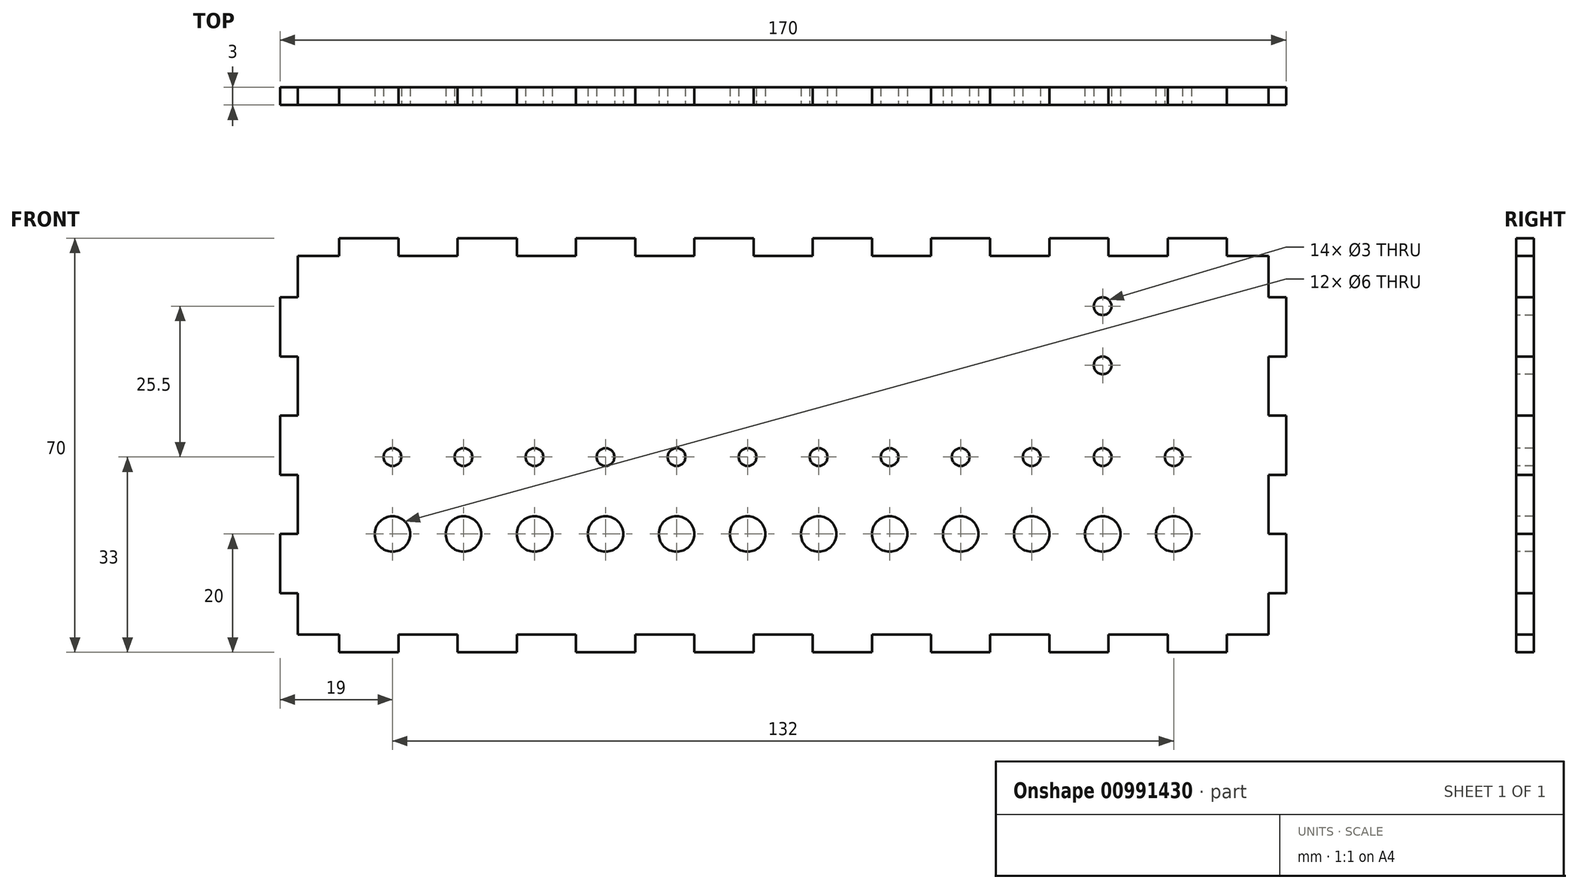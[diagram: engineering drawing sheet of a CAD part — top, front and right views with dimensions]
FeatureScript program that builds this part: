
annotation { "Feature Type Name" : "Feature", "Feature Type Description" : "" }
export const myFeature = defineFeature(function(context is Context, id is Id, definition is map)
    precondition{}
    {
        {
            var Q0;
            Q0=qCreatedBy(makeId("Front.planeOp"),FACE);
            var sketch = newSketch(context, id + "F0", { "sketchPlane" : qUnion([Q0])});
            skLineSegment(sketch, "E0.bottom", {"start": v(85, -35) * mm, "end": v(-85, -35) * mm});
            skLineSegment(sketch, "E0.top", {"start": v(85, 35) * mm, "end": v(-85, 35) * mm});
            skLineSegment(sketch, "E0.left", {"start": v(85, -35) * mm, "end": v(85, 35) * mm});
            skLineSegment(sketch, "E0.right", {"start": v(-85, -35) * mm, "end": v(-85, 35) * mm});
            skPoint(sketch, "E0.middle", {"position": v(0, 0) * mm});
            skSolve(sketch);
        }
        {
            var Q0;
            Q0=makeQuery(id+"F0.imprint","IMPRINT",FACE,{"disambiguationData":[TD([[makeQuery(id+"F0.imprint","IMPRINT",EDGE,{"derivedFrom":sQuery(id+"F0.wireOp",EDGE,"E0.bottom")}),-1.0]])]});
            extrude(context, id + "F1", {"entities" : qUnion([Q0]), "depth" : 3 * mm, "offsetDistance" : 25 * mm});
        }
        {
            var Q0;
            Q0=makeQuery(id+"F1.opExtrude","CAP_FACE",FACE,{"disambiguationData":[OSD([sQuery(id+"F0.wireOp",EDGE,"E0.bottom"),sQuery(id+"F0.wireOp",EDGE,"E0.top"),sQuery(id+"F0.wireOp",EDGE,"E0.left"),sQuery(id+"F0.wireOp",EDGE,"E0.right")])],"isStart":false});
            var sketch = newSketch(context, id + "F2", { "sketchPlane" : qUnion([Q0])});
            skLineSegment(sketch, "E1", {"start": v(-85, -15) * mm, "end": v(85, -15) * mm, "construction": true});
            skCircle(sketch, "E2", {"center": v(66, -15) * mm, "radius": 3 * mm});
            skCircle(sketch, "E3.1.0.0", {"center": v(54, -15) * mm, "radius": 3 * mm});
            skCircle(sketch, "E3.2.0.0", {"center": v(42, -15) * mm, "radius": 3 * mm});
            skCircle(sketch, "E3.3.0.0", {"center": v(30, -15) * mm, "radius": 3 * mm});
            skCircle(sketch, "E3.4.0.0", {"center": v(18, -15) * mm, "radius": 3 * mm});
            skCircle(sketch, "E3.5.0.0", {"center": v(6, -15) * mm, "radius": 3 * mm});
            skCircle(sketch, "E3.6.0.0", {"center": v(-6, -15) * mm, "radius": 3 * mm});
            skCircle(sketch, "E3.7.0.0", {"center": v(-18, -15) * mm, "radius": 3 * mm});
            skCircle(sketch, "E3.8.0.0", {"center": v(-30, -15) * mm, "radius": 3 * mm});
            skCircle(sketch, "E3.9.0.0", {"center": v(-42, -15) * mm, "radius": 3 * mm});
            skCircle(sketch, "E3.10.0.0", {"center": v(-54, -15) * mm, "radius": 3 * mm});
            skCircle(sketch, "E3.11.0.0", {"center": v(-66, -15) * mm, "radius": 3 * mm});
            skLineSegment(sketch, "E3.direction1", {"start": v(66, -15) * mm, "end": v(54, -15) * mm, "construction": true});
            skSolve(sketch);
        }
        {
            var Q0;
            Q0 = qSketchRegion(id + "F2", true);
            extrude(context, id + "F3", {"entities" : qUnion([Q0]), "operationType" : NewBodyOperationType.REMOVE, "endBound" : BoundingType.THROUGH_ALL, "oppositeDirection" : true, "depth" : 25 * mm, "offsetDistance" : 25 * mm});
        }
        {
            var Q0;
            Q0=makeQuery(id+"F1.opExtrude","CAP_FACE",FACE,{"disambiguationData":[OSD([sQuery(id+"F0.wireOp",EDGE,"E0.bottom"),sQuery(id+"F0.wireOp",EDGE,"E0.top"),sQuery(id+"F0.wireOp",EDGE,"E0.left"),sQuery(id+"F0.wireOp",EDGE,"E0.right")])],"isStart":false});
            var sketch = newSketch(context, id + "F4", { "sketchPlane" : qUnion([Q0])});
            skLineSegment(sketch, "E4", {"start": v(-85, -2) * mm, "end": v(85, -2) * mm, "construction": true});
            skLineSegment(sketch, "E5", {"start": v(-66, -15) * mm, "end": v(-66, -2) * mm, "construction": true});
            skCircle(sketch, "E6", {"center": v(-66, -2) * mm, "radius": 1.5 * mm});
            skCircle(sketch, "E7.1.0.0", {"center": v(-54, -2) * mm, "radius": 1.5 * mm});
            skCircle(sketch, "E7.2.0.0", {"center": v(-42, -2) * mm, "radius": 1.5 * mm});
            skCircle(sketch, "E7.3.0.0", {"center": v(-30, -2) * mm, "radius": 1.5 * mm});
            skCircle(sketch, "E7.4.0.0", {"center": v(-18, -2) * mm, "radius": 1.5 * mm});
            skCircle(sketch, "E7.5.0.0", {"center": v(-6, -2) * mm, "radius": 1.5 * mm});
            skCircle(sketch, "E7.6.0.0", {"center": v(6, -2) * mm, "radius": 1.5 * mm});
            skCircle(sketch, "E7.7.0.0", {"center": v(18, -2) * mm, "radius": 1.5 * mm});
            skCircle(sketch, "E7.8.0.0", {"center": v(30, -2) * mm, "radius": 1.5 * mm});
            skCircle(sketch, "E7.9.0.0", {"center": v(42, -2) * mm, "radius": 1.5 * mm});
            skCircle(sketch, "E7.10.0.0", {"center": v(54, -2) * mm, "radius": 1.5 * mm});
            skCircle(sketch, "E7.11.0.0", {"center": v(66, -2) * mm, "radius": 1.5 * mm});
            skLineSegment(sketch, "E7.direction1", {"start": v(-66, -2) * mm, "end": v(-54, -2) * mm, "construction": true});
            skSolve(sketch);
        }
        {
            var Q0;
            Q0 = qSketchRegion(id + "F4", true);
            extrude(context, id + "F5", {"entities" : qUnion([Q0]), "operationType" : NewBodyOperationType.REMOVE, "endBound" : BoundingType.THROUGH_ALL, "oppositeDirection" : true, "depth" : 25 * mm, "offsetDistance" : 25 * mm});
        }
        {
            var Q0;
            Q0=makeQuery(id+"F1.opExtrude","CAP_FACE",FACE,{"disambiguationData":[OSD([sQuery(id+"F0.wireOp",EDGE,"E0.bottom"),sQuery(id+"F0.wireOp",EDGE,"E0.top"),sQuery(id+"F0.wireOp",EDGE,"E0.left"),sQuery(id+"F0.wireOp",EDGE,"E0.right")])],"isStart":false});
            var sketch = newSketch(context, id + "F6", { "sketchPlane" : qUnion([Q0])});
            skLineSegment(sketch, "E8", {"start": v(54, -2) * mm, "end": v(54, 8.14) * mm, "construction": true});
            skCircle(sketch, "E9", {"center": v(54, 13.5) * mm, "radius": 1.5 * mm});
            skCircle(sketch, "E10.0.1.0", {"center": v(54, 23.5) * mm, "radius": 1.5 * mm});
            skLineSegment(sketch, "E10.direction1", {"start": v(54, 13.5) * mm, "end": v(79, 13.5) * mm, "construction": true});
            skLineSegment(sketch, "E10.direction2", {"start": v(54, 13.5) * mm, "end": v(54, 23.5) * mm, "construction": true});
            skSolve(sketch);
        }
        {
            var Q0;
            Q0 = qSketchRegion(id + "F6", true);
            extrude(context, id + "F7", {"entities" : qUnion([Q0]), "operationType" : NewBodyOperationType.REMOVE, "endBound" : BoundingType.THROUGH_ALL, "oppositeDirection" : true, "depth" : 25 * mm, "offsetDistance" : 25 * mm});
        }
        {
            var Q0;
            Q0=makeQuery(id+"F1.opExtrude","CAP_FACE",FACE,{"disambiguationData":[OSD([sQuery(id+"F0.wireOp",EDGE,"E0.bottom"),sQuery(id+"F0.wireOp",EDGE,"E0.top"),sQuery(id+"F0.wireOp",EDGE,"E0.left"),sQuery(id+"F0.wireOp",EDGE,"E0.right")])],"isStart":false});
            var sketch = newSketch(context, id + "F8", { "sketchPlane" : qUnion([Q0])});
            skLineSegment(sketch, "E11.bottom", {"start": v(-85, -35) * mm, "end": v(-75, -35) * mm});
            skLineSegment(sketch, "E11.top", {"start": v(-85, -32) * mm, "end": v(-75, -32) * mm});
            skLineSegment(sketch, "E11.left", {"start": v(-85, -35) * mm, "end": v(-85, -32) * mm});
            skLineSegment(sketch, "E11.right", {"start": v(-75, -35) * mm, "end": v(-75, -32) * mm});
            skLineSegment(sketch, "E12.1.0.0", {"start": v(-55, -35) * mm, "end": v(-55, -32) * mm});
            skLineSegment(sketch, "E12.1.0.1", {"start": v(-65, -35) * mm, "end": v(-65, -32) * mm});
            skLineSegment(sketch, "E12.1.0.2", {"start": v(-65, -35) * mm, "end": v(-55, -35) * mm});
            skLineSegment(sketch, "E12.1.0.3", {"start": v(-65, -32) * mm, "end": v(-55, -32) * mm});
            skLineSegment(sketch, "E12.2.0.0", {"start": v(-35, -35) * mm, "end": v(-35, -32) * mm});
            skLineSegment(sketch, "E12.2.0.1", {"start": v(-45, -35) * mm, "end": v(-45, -32) * mm});
            skLineSegment(sketch, "E12.2.0.2", {"start": v(-45, -35) * mm, "end": v(-35, -35) * mm});
            skLineSegment(sketch, "E12.2.0.3", {"start": v(-45, -32) * mm, "end": v(-35, -32) * mm});
            skLineSegment(sketch, "E12.3.0.0", {"start": v(-15, -35) * mm, "end": v(-15, -32) * mm});
            skLineSegment(sketch, "E12.3.0.1", {"start": v(-25, -35) * mm, "end": v(-25, -32) * mm});
            skLineSegment(sketch, "E12.3.0.2", {"start": v(-25, -35) * mm, "end": v(-15, -35) * mm});
            skLineSegment(sketch, "E12.3.0.3", {"start": v(-25, -32) * mm, "end": v(-15, -32) * mm});
            skLineSegment(sketch, "E12.4.0.0", {"start": v(5, -35) * mm, "end": v(5, -32) * mm});
            skLineSegment(sketch, "E12.4.0.1", {"start": v(-5, -35) * mm, "end": v(-5, -32) * mm});
            skLineSegment(sketch, "E12.4.0.2", {"start": v(-5, -35) * mm, "end": v(5, -35) * mm});
            skLineSegment(sketch, "E12.4.0.3", {"start": v(-5, -32) * mm, "end": v(5, -32) * mm});
            skLineSegment(sketch, "E12.5.0.0", {"start": v(25, -35) * mm, "end": v(25, -32) * mm});
            skLineSegment(sketch, "E12.5.0.1", {"start": v(15, -35) * mm, "end": v(15, -32) * mm});
            skLineSegment(sketch, "E12.5.0.2", {"start": v(15, -35) * mm, "end": v(25, -35) * mm});
            skLineSegment(sketch, "E12.5.0.3", {"start": v(15, -32) * mm, "end": v(25, -32) * mm});
            skLineSegment(sketch, "E12.6.0.0", {"start": v(45, -35) * mm, "end": v(45, -32) * mm});
            skLineSegment(sketch, "E12.6.0.1", {"start": v(35, -35) * mm, "end": v(35, -32) * mm});
            skLineSegment(sketch, "E12.6.0.2", {"start": v(35, -35) * mm, "end": v(45, -35) * mm});
            skLineSegment(sketch, "E12.6.0.3", {"start": v(35, -32) * mm, "end": v(45, -32) * mm});
            skLineSegment(sketch, "E12.7.0.0", {"start": v(65, -35) * mm, "end": v(65, -32) * mm});
            skLineSegment(sketch, "E12.7.0.1", {"start": v(55, -35) * mm, "end": v(55, -32) * mm});
            skLineSegment(sketch, "E12.7.0.2", {"start": v(55, -35) * mm, "end": v(65, -35) * mm});
            skLineSegment(sketch, "E12.7.0.3", {"start": v(55, -32) * mm, "end": v(65, -32) * mm});
            skLineSegment(sketch, "E12.8.0.0", {"start": v(85, -35) * mm, "end": v(85, -32) * mm});
            skLineSegment(sketch, "E12.8.0.1", {"start": v(75, -35) * mm, "end": v(75, -32) * mm});
            skLineSegment(sketch, "E12.8.0.2", {"start": v(75, -35) * mm, "end": v(85, -35) * mm});
            skLineSegment(sketch, "E12.8.0.3", {"start": v(75, -32) * mm, "end": v(85, -32) * mm});
            skLineSegment(sketch, "E12.direction1", {"start": v(-85, -35) * mm, "end": v(-65, -35) * mm, "construction": true});
            skLineSegment(sketch, "E13", {"start": v(-85, 0) * mm, "end": v(85, 0) * mm, "construction": true});
            skLineSegment(sketch, "E14.MirrorCS", {"start": v(-65, 35) * mm, "end": v(-65, 32) * mm});
            skLineSegment(sketch, "E15.MirrorCS", {"start": v(-25, 35) * mm, "end": v(-25, 32) * mm});
            skLineSegment(sketch, "E16.MirrorCS", {"start": v(-35, 35) * mm, "end": v(-35, 32) * mm});
            skLineSegment(sketch, "E17.MirrorCS", {"start": v(-5, 35) * mm, "end": v(-5, 32) * mm});
            skLineSegment(sketch, "E18.MirrorCS", {"start": v(-85, 35) * mm, "end": v(-85, 32) * mm});
            skLineSegment(sketch, "E19.MirrorCS", {"start": v(75, 35) * mm, "end": v(75, 32) * mm});
            skLineSegment(sketch, "E20.MirrorCS", {"start": v(25, 35) * mm, "end": v(25, 32) * mm});
            skLineSegment(sketch, "E21.MirrorCS", {"start": v(-45, 35) * mm, "end": v(-45, 32) * mm});
            skLineSegment(sketch, "E22.MirrorCS", {"start": v(45, 35) * mm, "end": v(45, 32) * mm});
            skLineSegment(sketch, "E23.MirrorCS", {"start": v(-55, 35) * mm, "end": v(-55, 32) * mm});
            skLineSegment(sketch, "E24.MirrorCS", {"start": v(85, 35) * mm, "end": v(85, 32) * mm});
            skLineSegment(sketch, "E25.MirrorCS", {"start": v(-15, 35) * mm, "end": v(-15, 32) * mm});
            skLineSegment(sketch, "E26.MirrorCS", {"start": v(55, 35) * mm, "end": v(55, 32) * mm});
            skLineSegment(sketch, "E27.MirrorCS", {"start": v(65, 35) * mm, "end": v(65, 32) * mm});
            skLineSegment(sketch, "E28.MirrorCS", {"start": v(15, 35) * mm, "end": v(15, 32) * mm});
            skLineSegment(sketch, "E29.MirrorCS", {"start": v(35, 35) * mm, "end": v(35, 32) * mm});
            skLineSegment(sketch, "E30.MirrorCS", {"start": v(5, 35) * mm, "end": v(5, 32) * mm});
            skLineSegment(sketch, "E31.MirrorCS", {"start": v(-75, 35) * mm, "end": v(-75, 32) * mm});
            skLineSegment(sketch, "E32.MirrorCS", {"start": v(-85, 35) * mm, "end": v(-75, 35) * mm});
            skLineSegment(sketch, "E33.MirrorCS", {"start": v(-25, 35) * mm, "end": v(-15, 35) * mm});
            skLineSegment(sketch, "E34.MirrorCS", {"start": v(55, 35) * mm, "end": v(65, 35) * mm});
            skLineSegment(sketch, "E35.MirrorCS", {"start": v(-25, 32) * mm, "end": v(-15, 32) * mm});
            skLineSegment(sketch, "E36.MirrorCS", {"start": v(35, 32) * mm, "end": v(45, 32) * mm});
            skLineSegment(sketch, "E37.MirrorCS", {"start": v(55, 32) * mm, "end": v(65, 32) * mm});
            skLineSegment(sketch, "E38.MirrorCS", {"start": v(15, 35) * mm, "end": v(25, 35) * mm});
            skLineSegment(sketch, "E39.MirrorCS", {"start": v(-65, 32) * mm, "end": v(-55, 32) * mm});
            skLineSegment(sketch, "E40.MirrorCS", {"start": v(35, 35) * mm, "end": v(45, 35) * mm});
            skLineSegment(sketch, "E41.MirrorCS", {"start": v(-45, 35) * mm, "end": v(-35, 35) * mm});
            skLineSegment(sketch, "E42.MirrorCS", {"start": v(75, 32) * mm, "end": v(85, 32) * mm});
            skLineSegment(sketch, "E43.MirrorCS", {"start": v(-5, 32) * mm, "end": v(5, 32) * mm});
            skLineSegment(sketch, "E44.MirrorCS", {"start": v(-65, 35) * mm, "end": v(-55, 35) * mm});
            skLineSegment(sketch, "E45.MirrorCS", {"start": v(-85, 35) * mm, "end": v(-65, 35) * mm, "construction": true});
            skLineSegment(sketch, "E46.MirrorCS", {"start": v(-45, 32) * mm, "end": v(-35, 32) * mm});
            skLineSegment(sketch, "E47.MirrorCS", {"start": v(-5, 35) * mm, "end": v(5, 35) * mm});
            skLineSegment(sketch, "E48.MirrorCS", {"start": v(-85, 32) * mm, "end": v(-75, 32) * mm});
            skLineSegment(sketch, "E49.MirrorCS", {"start": v(75, 35) * mm, "end": v(85, 35) * mm});
            skLineSegment(sketch, "E50.MirrorCS", {"start": v(15, 32) * mm, "end": v(25, 32) * mm});
            skLineSegment(sketch, "E51.bottom", {"start": v(-85, 35) * mm, "end": v(-82, 35) * mm});
            skLineSegment(sketch, "E51.top", {"start": v(-85, 25) * mm, "end": v(-82, 25) * mm});
            skLineSegment(sketch, "E51.left", {"start": v(-85, 35) * mm, "end": v(-85, 25) * mm});
            skLineSegment(sketch, "E51.right", {"start": v(-82, 35) * mm, "end": v(-82, 25) * mm});
            skLineSegment(sketch, "E52.0.1.0", {"start": v(-82, 15) * mm, "end": v(-82, 5) * mm});
            skLineSegment(sketch, "E52.0.1.1", {"start": v(-85, 15) * mm, "end": v(-85, 5) * mm});
            skLineSegment(sketch, "E52.0.1.2", {"start": v(-85, 5) * mm, "end": v(-82, 5) * mm});
            skLineSegment(sketch, "E52.0.1.3", {"start": v(-85, 15) * mm, "end": v(-82, 15) * mm});
            skLineSegment(sketch, "E52.0.1.4", {"start": v(-85, 15) * mm, "end": v(-85, 12) * mm});
            skLineSegment(sketch, "E52.0.2.0", {"start": v(-82, -5) * mm, "end": v(-82, -15) * mm});
            skLineSegment(sketch, "E52.0.2.1", {"start": v(-85, -5) * mm, "end": v(-85, -15) * mm});
            skLineSegment(sketch, "E52.0.2.2", {"start": v(-85, -15) * mm, "end": v(-82, -15) * mm});
            skLineSegment(sketch, "E52.0.2.3", {"start": v(-85, -5) * mm, "end": v(-82, -5) * mm});
            skLineSegment(sketch, "E52.0.2.4", {"start": v(-85, -5) * mm, "end": v(-85, -8) * mm});
            skLineSegment(sketch, "E52.0.3.0", {"start": v(-82, -25) * mm, "end": v(-82, -35) * mm});
            skLineSegment(sketch, "E52.0.3.1", {"start": v(-85, -25) * mm, "end": v(-85, -35) * mm});
            skLineSegment(sketch, "E52.0.3.2", {"start": v(-85, -35) * mm, "end": v(-82, -35) * mm});
            skLineSegment(sketch, "E52.0.3.3", {"start": v(-85, -25) * mm, "end": v(-82, -25) * mm});
            skLineSegment(sketch, "E52.0.3.4", {"start": v(-85, -25) * mm, "end": v(-85, -28) * mm});
            skLineSegment(sketch, "E52.direction1", {"start": v(-85, 25) * mm, "end": v(-60, 25) * mm, "construction": true});
            skLineSegment(sketch, "E52.direction2", {"start": v(-85, 25) * mm, "end": v(-85, 5) * mm, "construction": true});
            skLineSegment(sketch, "E53", {"start": v(0, 35) * mm, "end": v(0, -35) * mm, "construction": true});
            skLineSegment(sketch, "E54.MirrorCS", {"start": v(85, -25) * mm, "end": v(85, -28) * mm});
            skLineSegment(sketch, "E55.MirrorCS", {"start": v(85, 15) * mm, "end": v(85, 12) * mm});
            skLineSegment(sketch, "E56.MirrorCS", {"start": v(85, -5) * mm, "end": v(85, -8) * mm});
            skLineSegment(sketch, "E57.MirrorCS", {"start": v(85, 15) * mm, "end": v(85, 5) * mm});
            skLineSegment(sketch, "E58.MirrorCS", {"start": v(85, 5) * mm, "end": v(82, 5) * mm});
            skLineSegment(sketch, "E59.MirrorCS", {"start": v(82, 15) * mm, "end": v(82, 5) * mm});
            skLineSegment(sketch, "E60.MirrorCS", {"start": v(85, -35) * mm, "end": v(82, -35) * mm});
            skLineSegment(sketch, "E61.MirrorCS", {"start": v(85, -5) * mm, "end": v(85, -15) * mm});
            skLineSegment(sketch, "E62.MirrorCS", {"start": v(85, 35) * mm, "end": v(82, 35) * mm});
            skLineSegment(sketch, "E63.MirrorCS", {"start": v(85, 25) * mm, "end": v(85, 5) * mm, "construction": true});
            skLineSegment(sketch, "E64.MirrorCS", {"start": v(82, -25) * mm, "end": v(82, -35) * mm});
            skLineSegment(sketch, "E65.MirrorCS", {"start": v(85, 15) * mm, "end": v(82, 15) * mm});
            skLineSegment(sketch, "E66.MirrorCS", {"start": v(85, -15) * mm, "end": v(82, -15) * mm});
            skLineSegment(sketch, "E67.MirrorCS", {"start": v(85, -25) * mm, "end": v(82, -25) * mm});
            skLineSegment(sketch, "E68.MirrorCS", {"start": v(85, 25) * mm, "end": v(82, 25) * mm});
            skLineSegment(sketch, "E69.MirrorCS", {"start": v(82, 35) * mm, "end": v(82, 25) * mm});
            skLineSegment(sketch, "E70.MirrorCS", {"start": v(85, 35) * mm, "end": v(85, 25) * mm});
            skLineSegment(sketch, "E71.MirrorCS", {"start": v(85, -25) * mm, "end": v(85, -35) * mm});
            skLineSegment(sketch, "E72.MirrorCS", {"start": v(85, -5) * mm, "end": v(82, -5) * mm});
            skLineSegment(sketch, "E73.MirrorCS", {"start": v(82, -5) * mm, "end": v(82, -15) * mm});
            skSolve(sketch);
        }
        {
            var Q0;
            Q0 = qSketchRegion(id + "F8", true);
            extrude(context, id + "F9", {"entities" : qUnion([Q0]), "operationType" : NewBodyOperationType.REMOVE, "endBound" : BoundingType.THROUGH_ALL, "oppositeDirection" : true, "depth" : 25 * mm, "offsetDistance" : 25 * mm});
        }
    });
